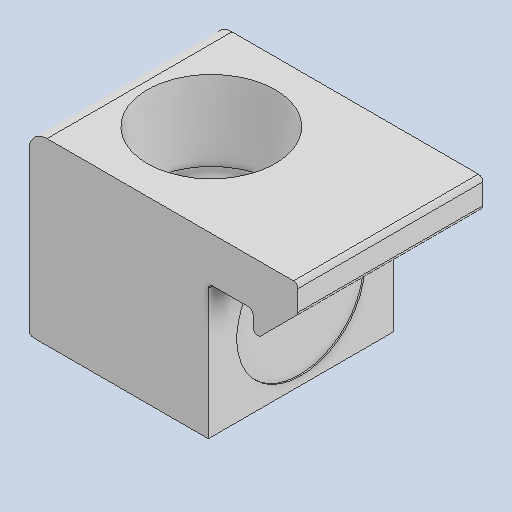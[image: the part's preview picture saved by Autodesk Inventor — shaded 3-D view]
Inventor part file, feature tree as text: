
AUTODESK INVENTOR PART (.ipt)
format: ipt  version: 2022 (Build 260153000, 153)  size: 129,536 bytes
history: native  units: in
note: dims shown in document units (in); Inventor stores cm internally (conversion verified against a paired STEP export)
features: fillet x1
ambient origin geometry x8: Origin, YZ Plane, XZ Plane, XY Plane, X Axis, Y Axis, Z Axis, Center Point
bodies: Solid1 (feature_tree)
feature tree (1):
  fillet  "Fillet2"  [1 undecoded]
note: 1 required parameter value undecoded (feature->parameter linkage not recoverable at this tier; creation-order binding heuristic only, values carry confidence <= 0.55)
